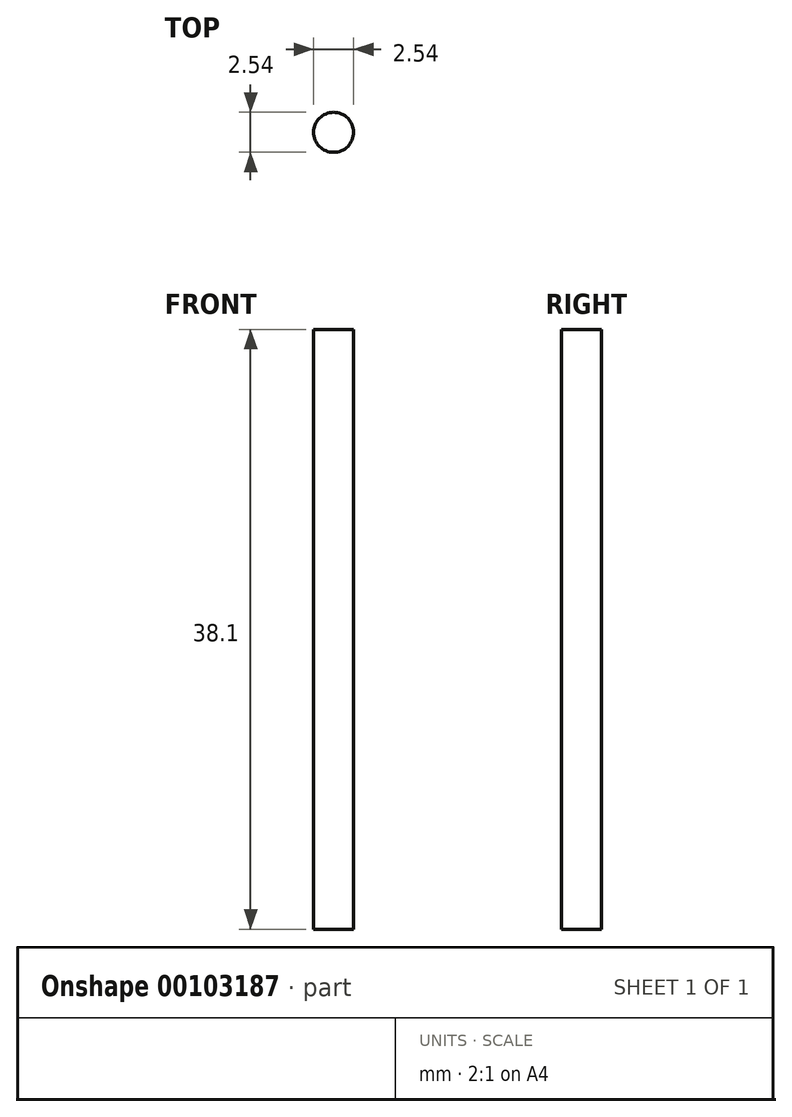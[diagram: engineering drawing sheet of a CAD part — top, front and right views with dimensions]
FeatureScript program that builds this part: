
annotation { "Feature Type Name" : "Feature", "Feature Type Description" : "" }
export const myFeature = defineFeature(function(context is Context, id is Id, definition is map)
    precondition{}
    {
        {
            var Q0;
            Q0=qCreatedBy(makeId("Top.planeOp"),FACE);
            var sketch = newSketch(context, id + "F0", { "sketchPlane" : qUnion([Q0])});
            skCircle(sketch, "E0", {"center": v(0, 0) * mm, "radius": 1.27 * mm});
            skSolve(sketch);
        }
        {
            var Q0;
            Q0=makeQuery(id+"F0.imprint","IMPRINT",FACE,{"disambiguationData":[TD([[makeQuery(id+"F0.imprint","IMPRINT",EDGE,{"derivedFrom":sQuery(id+"F0.wireOp",EDGE,"E0")}),1.0]])]});
            extrude(context, id + "F1", {"entities" : qUnion([Q0]), "endBound" : BoundingType.SYMMETRIC, "depth" : 38.1 * mm});
        }
    });
